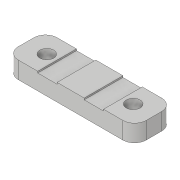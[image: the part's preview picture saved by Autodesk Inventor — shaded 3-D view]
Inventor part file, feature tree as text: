
AUTODESK INVENTOR PART (.ipt)
format: ipt  version: 2020 (Build 240168000, 168)  size: 246,272 bytes
history: native  units: in
note: dims shown in document units (in); Inventor stores cm internally (conversion verified against a paired STEP export)
features: extrude x5, sketch x5, mirror x2, plane x1, fillet x1
ambient origin geometry x8: Origin, YZ Plane, XZ Plane, XY Plane, X Axis, Y Axis, Z Axis, Center Point
bodies: Solid1 (feature_tree)
feature tree (14):
  extrude  "Extrusion1"  Depth=0.3937in
  extrude  "Extrusion2"  Depth=0.1575in TaperAngle=0.0deg
  plane  "Work Plane1"
  mirror  "Mirror1"
  fillet  "Fillet1"  [1 undecoded]
  extrude  "Extrusion3"  Depth=0.1417in
  extrude  "Extrusion4"  Depth=0.3937in
  mirror  "Mirror2"
  extrude  "Extrusion5"  Depth=0.315in
  sketch  "Sketch1"  dims[d0=1.2992in d1=0.3937in]
  sketch  "Sketch2"  dims[d2=0.1575in d3=0.0in d5=0.1575in d6=0.0in d7=-0.6496in]
  sketch  "Sketch3"  dims[d8=0.1181in d9=0.1417in]
  sketch  "Sketch4"  dims[d10=0.2756in d11=0.3937in]
  sketch  "Sketch5"  dims[d12=0.0157in d13=0.0in d14=0.315in d15=0.3937in d16=0.1181in d17=0.0157in d18=0.0in d19=0.0197in d20=0.0in]
note: 1 required parameter value undecoded (feature->parameter linkage not recoverable at this tier; creation-order binding heuristic only, values carry confidence <= 0.55)
